# Revit family: 303_R401X_
name_source: partatom
category: Pipe Accessories
revit_build: Autodesk Revit 2018 (Build: 20170223_1515(x64)
units: mm (PartAtom-declared; Revit-internal decimal feet)

## family parameters
Always vertical = Yes
Cut with Voids When Loaded = No
Part Type = Valve - Breaks Into
Round Connector Dimension = Use Diameter
Shared = No
Work Plane-Based = No

## types (4) — shared parameters
CAT0 = Yes
CAT1 = No
Description = Angle valve with thermostatic option
J2 = 2 mm  [stored 0.00656168 ft]
L2D_Min = 3048 mm
M1 = 12 mm  [stored 0.0393701 ft]
M3 = 17 mm
M3__ve = -17 mm
Manufacturer = Giacomini
QmdConnectorList = 301;D;302;D1
SW2 = No
URL = http://www.giacomini.com
X1 = 17 mm
X2 = 14 mm  [stored 0.0459318 ft]
magiPartTypeId = 303
magiProductFamilyId = R401X*
zero-valued in all types: MC_Default_elevation

## per-type parameters (varying)
- R401X132: B1=6 mm  [stored 0.019685 ft]; B4=9 mm  [stored 0.0295276 ft]; CenSd_K1_6=10 mm  [stored 0.0328084 ft]; CenSd_W2_6=12 mm  [stored 0.0393701 ft]; D=10 mm; D1=10 mm; G1=8 mm  [stored 0.0262467 ft]; G3=10 mm  [stored 0.0328084 ft]; H3=3 mm  [stored 0.00984252 ft]; H3__ve=-3 mm  [stored -0.00984252 ft]; H4=1 mm  [stored 0.00328084 ft]; HLL=11 mm  [stored 0.0360892 ft]; J=20 mm  [stored 0.0656168 ft]; J1=6 mm  [stored 0.019685 ft]; J11=23 mm; J12=8 mm  [stored 0.0262467 ft]; J13=4 mm  [stored 0.0131234 ft]; J1__ve=-6 mm; J4=6 mm  [stored 0.019685 ft]; K1=11 mm  [stored 0.0360892 ft]; KH=10 mm  [stored 0.0328084 ft]; KH__ve=-10 mm  [stored -0.0328084 ft]; L=38 mm  [stored 0.124672 ft]; L1=7 mm  [stored 0.0229659 ft]; L1__ve=-7 mm  [stored -0.0229659 ft]; L2D=38 mm  [stored 0.124672 ft]; LX=51 mm; R1=8 mm  [stored 0.0262467 ft]; SW1=No; SW3=Yes; SW4=Yes; W1=11 mm  [stored 0.0360892 ft]; W2=14 mm  [stored 0.0459318 ft]; W2D=10 mm  [stored 0.0328084 ft]; X3=5 mm  [stored 0.0164042 ft]; X4=4 mm  [stored 0.0131234 ft]; X41=3 mm  [stored 0.00984252 ft]; X41__ve=-3 mm  [stored -0.00984252 ft]; X4__ve=-4 mm  [stored -0.0131234 ft]
- R401X035: B1=11 mm  [stored 0.0360892 ft]; B4=17 mm; CenSd_K1_6=17 mm; CenSd_W2_6=20 mm  [stored 0.0656168 ft]; D=25 mm; D1=25 mm; G1=15 mm  [stored 0.0492126 ft]; G3=17 mm; H3=6 mm  [stored 0.019685 ft]; H3__ve=-6 mm; H4=3 mm  [stored 0.00984252 ft]; HLL=20 mm  [stored 0.0656168 ft]; J=31 mm; J1=8 mm  [stored 0.0262467 ft]; J11=31 mm; J12=10 mm  [stored 0.0328084 ft]; J13=5 mm  [stored 0.0164042 ft]; J1__ve=-8 mm  [stored -0.0262467 ft]; J4=8 mm  [stored 0.0262467 ft]; K1=20 mm  [stored 0.0656168 ft]; KH=16 mm; KH__ve=-16 mm; L=53 mm; L1=13 mm; L1__ve=-13 mm; L2D=53 mm; LX=71 mm; R1=16 mm; SW1=Yes; SW3=No; SW4=No; W1=18 mm; W2=23 mm; W2D=25 mm  [stored 0.082021 ft]; X3=8 mm  [stored 0.0262467 ft]; X4=7 mm  [stored 0.0229659 ft]; X41=6 mm  [stored 0.019685 ft]; X41__ve=-6 mm; X4__ve=-7 mm  [stored -0.0229659 ft]
- R401X034: B1=9 mm  [stored 0.0295276 ft]; B4=14 mm  [stored 0.0459318 ft]; CenSd_K1_6=14 mm  [stored 0.0459318 ft]; CenSd_W2_6=16 mm; D=20 mm; D1=20 mm; G1=13 mm; G3=15 mm  [stored 0.0492126 ft]; H3=5 mm  [stored 0.0164042 ft]; H3__ve=-5 mm  [stored -0.0164042 ft]; H4=2 mm  [stored 0.00656168 ft]; HLL=15 mm  [stored 0.0492126 ft]; J=25 mm  [stored 0.082021 ft]; J1=6 mm  [stored 0.019685 ft]; J11=23 mm; J12=8 mm  [stored 0.0262467 ft]; J13=4 mm  [stored 0.0131234 ft]; J1__ve=-6 mm; J4=6 mm  [stored 0.019685 ft]; K1=16 mm; KH=13 mm; KH__ve=-13 mm; L=45 mm; L1=10 mm  [stored 0.0328084 ft]; L1__ve=-10 mm  [stored -0.0328084 ft]; L2D=45 mm; LX=60 mm; R1=13 mm; SW1=Yes; SW3=No; SW4=No; W1=15 mm  [stored 0.0492126 ft]; W2=19 mm  [stored 0.062336 ft]; W2D=20 mm  [stored 0.0656168 ft]; X3=7 mm  [stored 0.0229659 ft]; X4=5 mm  [stored 0.0164042 ft]; X41=4 mm  [stored 0.0131234 ft]; X41__ve=-4 mm  [stored -0.0131234 ft]; X4__ve=-5 mm  [stored -0.0164042 ft]
- R401X133: B1=7 mm  [stored 0.0229659 ft]; B4=11 mm  [stored 0.0360892 ft]; CenSd_K1_6=11 mm  [stored 0.0360892 ft]; CenSd_W2_6=13 mm; D=15 mm; D1=15 mm; G1=10 mm  [stored 0.0328084 ft]; G3=12 mm  [stored 0.0393701 ft]; H3=4 mm  [stored 0.0131234 ft]; H3__ve=-4 mm  [stored -0.0131234 ft]; H4=2 mm  [stored 0.00656168 ft]; HLL=12 mm  [stored 0.0393701 ft]; J=23 mm; J1=6 mm  [stored 0.019685 ft]; J11=24 mm  [stored 0.0787402 ft]; J12=8 mm  [stored 0.0262467 ft]; J13=4 mm  [stored 0.0131234 ft]; J1__ve=-6 mm; J4=6 mm  [stored 0.019685 ft]; K1=13 mm; KH=12 mm  [stored 0.0393701 ft]; KH__ve=-12 mm; L=40 mm; L1=8 mm  [stored 0.0262467 ft]; L1__ve=-8 mm  [stored -0.0262467 ft]; L2D=40 mm; LX=53 mm; R1=11 mm  [stored 0.0360892 ft]; SW1=No; SW3=Yes; SW4=Yes; W1=12 mm  [stored 0.0393701 ft]; W2=15 mm  [stored 0.0492126 ft]; W2D=15 mm  [stored 0.0492126 ft]; X3=6 mm  [stored 0.019685 ft]; X4=4 mm  [stored 0.0131234 ft]; X41=3 mm  [stored 0.00984252 ft]; X41__ve=-3 mm  [stored -0.00984252 ft]; X4__ve=-4 mm  [stored -0.0131234 ft]

note: column(s) folded — value = type name in every type: magiProductCode, magiProductId

note: [stored X ft] marks values corroborated as IEEE doubles in the binary element streams (Revit-internal decimal feet)

## geometry (parser evidence)
native form markers: Sweep x2
no freeform markers — native parametric forms only
